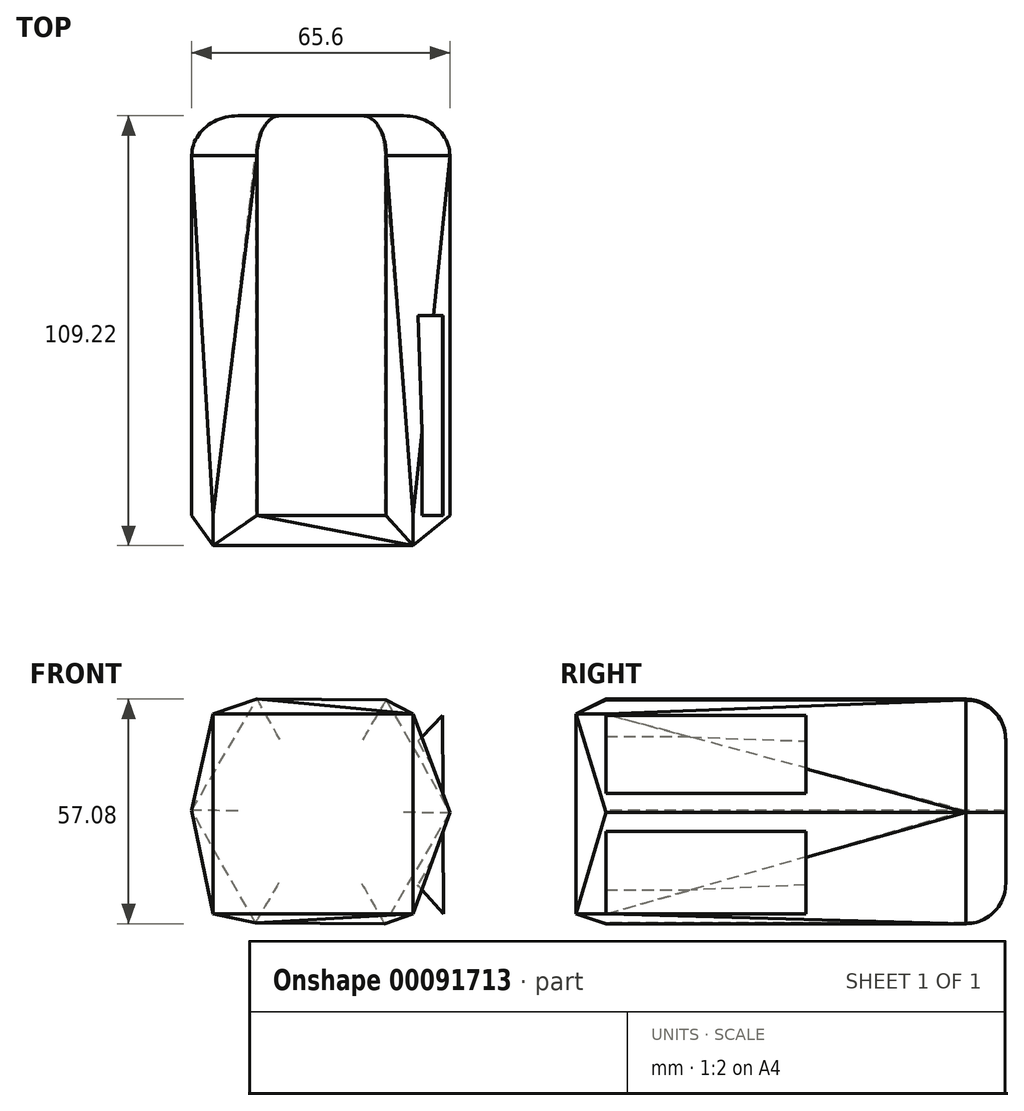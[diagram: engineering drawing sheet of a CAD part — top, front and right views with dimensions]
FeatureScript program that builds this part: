
annotation { "Feature Type Name" : "Feature", "Feature Type Description" : "" }
export const myFeature = defineFeature(function(context is Context, id is Id, definition is map)
    precondition{}
    {
        {
            var Q0;
            Q0=qCreatedBy(makeId("Front.planeOp"),FACE);
            var sketch = newSketch(context, id + "F0", { "sketchPlane" : qUnion([Q0])});
            skCircle(sketch, "E0.cCircle", {"center": v(0, 0) * mm, "radius": 32.8 * mm, "construction": true});
            skLineSegment(sketch, "E0.0", {"start": v(16.18, -28.54) * mm, "end": v(-16.62, -28.28) * mm});
            skLineSegment(sketch, "E0.1", {"start": v(-16.62, -28.28) * mm, "end": v(-32.8, 0.25) * mm});
            skLineSegment(sketch, "E0.2", {"start": v(-32.8, 0.25) * mm, "end": v(-16.18, 28.54) * mm});
            skLineSegment(sketch, "E0.3", {"start": v(-16.18, 28.54) * mm, "end": v(16.62, 28.28) * mm});
            skLineSegment(sketch, "E0.4", {"start": v(16.62, 28.28) * mm, "end": v(32.8, -0.25) * mm});
            skLineSegment(sketch, "E0.5", {"start": v(32.8, -0.25) * mm, "end": v(16.18, -28.54) * mm});
            skSolve(sketch);
        }
        {
            var Q0;
            Q0=makeQuery(id+"F0.imprint","IMPRINT",FACE,{"disambiguationData":[TD([[makeQuery(id+"F0.imprint","IMPRINT",EDGE,{"derivedFrom":sQuery(id+"F0.wireOp",EDGE,"E0.0")}),-1.0]])]});
            extrude(context, id + "F1", {"entities" : qUnion([Q0]), "oppositeDirection" : true, "depth" : 101.6 * mm});
        }
        {
            var Q0;
            Q0=makeQuery(id+"F1.opExtrude","CAP_EDGE",EDGE,{"disambiguationData":[OSD([sQuery(id+"F0.wireOp",EDGE,"E0.5")])],"isStart":false});
            var Q1;
            Q1=makeQuery(id+"F1.opExtrude","CAP_EDGE",EDGE,{"disambiguationData":[OSD([sQuery(id+"F0.wireOp",EDGE,"E0.4")])],"isStart":false});
            var Q2;
            Q2=makeQuery(id+"F1.opExtrude","CAP_EDGE",EDGE,{"disambiguationData":[OSD([sQuery(id+"F0.wireOp",EDGE,"E0.3")])],"isStart":false});
            var Q3;
            Q3=makeQuery(id+"F1.opExtrude","CAP_EDGE",EDGE,{"disambiguationData":[OSD([sQuery(id+"F0.wireOp",EDGE,"E0.2")])],"isStart":false});
            var Q4;
            Q4=makeQuery(id+"F1.opExtrude","CAP_EDGE",EDGE,{"disambiguationData":[OSD([sQuery(id+"F0.wireOp",EDGE,"E0.1")])],"isStart":false});
            var Q5;
            Q5=makeQuery(id+"F1.opExtrude","CAP_EDGE",EDGE,{"disambiguationData":[OSD([sQuery(id+"F0.wireOp",EDGE,"E0.0")])],"isStart":false});
            fillet(context, id + "F2", {"entities" : qUnion([Q0, Q1, Q2, Q3, Q4, Q5]), "radius" : 10.16 * mm, "tangentPropagation" : true, "allowEdgeOverflow" : false});
        }
        {
            var Q0;
            Q0=qCreatedBy(makeId("Front.planeOp"),FACE);
            var sketch = newSketch(context, id + "F3", { "sketchPlane" : qUnion([Q0])});
            skLineSegment(sketch, "E1.bottom", {"start": v(-27.3, 24.74) * mm, "end": v(23.5, 24.74) * mm});
            skLineSegment(sketch, "E1.top", {"start": v(-27.3, -26.06) * mm, "end": v(23.5, -26.06) * mm});
            skLineSegment(sketch, "E1.left", {"start": v(-27.3, 24.74) * mm, "end": v(-27.3, -26.06) * mm});
            skLineSegment(sketch, "E1.right", {"start": v(23.5, 24.74) * mm, "end": v(23.5, -26.06) * mm});
            skSolve(sketch);
        }
        {
            var Q0;
            Q0=makeQuery(id+"F3.imprint","IMPRINT",FACE,{"disambiguationData":[TD([[makeQuery(id+"F3.imprint","IMPRINT",EDGE,{"derivedFrom":sQuery(id+"F3.wireOp",EDGE,"E1.bottom")}),-1.0]])]});
            extrude(context, id + "F4", {"entities" : qUnion([Q0]), "operationType" : NewBodyOperationType.ADD, "depth" : 7.62 * mm});
        }
        {
            var Q1;
            Q1=makeQuery(id+"F1.opExtrude","CAP_VERTEX",VERTEX,{"disambiguationData":[OSD([sQuery(id+"F0.wireOp",EDGE,"E0.0"),sQuery(id+"F0.wireOp",EDGE,"E0.1")])],"isStart":true});
            var Q2;
            Q2=makeQuery(id+"F4.opExtrude","SWEPT_FACE",FACE,{"disambiguationData":[OSD([sQuery(id+"F3.wireOp",EDGE,"E1.top")])]});
            loft(context, id + "F5", {"operationType" : NewBodyOperationType.ADD, "sheetProfilesArray" : [{ "sheetProfileEntities" : qUnion([Q1]) }, { "sheetProfileEntities" : qUnion([Q2]) }]});
        }
        {
            var Q1;
            Q1=makeQuery(id+"F1.opExtrude","CAP_VERTEX",VERTEX,{"disambiguationData":[OSD([sQuery(id+"F0.wireOp",EDGE,"E0.0"),sQuery(id+"F0.wireOp",EDGE,"E0.5")])],"isStart":true});
            var Q2;
            Q2=makeQuery(id+"F5.opLoft","SWEPT_FACE",FACE,{"disambiguationData":[OSD([sQuery(id+"F3.wireOp",EDGE,"E1.top"),sQuery(id+"F3.wireOp",EDGE,"E1.right")])]});
            loft(context, id + "F6", {"operationType" : NewBodyOperationType.ADD, "sheetProfilesArray" : [{ "sheetProfileEntities" : qUnion([Q1]) }, { "sheetProfileEntities" : qUnion([Q2]) }]});
        }
        {
            var Q1;
            {var subQ0=sQuery(id+"F3.wireOp",EDGE,"E1.left");var subQ1=sQuery(id+"F3.wireOp",EDGE,"E1.top");var subQ2=makeQuery(id+"F4.opExtrude","CAP_VERTEX",VERTEX,{"disambiguationData":[OSD([subQ1,subQ0])],"isStart":true});Q1=makeQuery(id+"F5.boolean.opBoolean","MERGE",VERTEX,{"derivedFrom":[subQ2,makeQuery(id+"F5.opLoft","MID_CAP_VERTEX",VERTEX,{"disambiguationData":[OSD([subQ1,subQ0]),TDD([subQ2])],"capPos":1.0})]});}
            var Q2;
            Q2=makeQuery(id+"F1.opExtrude","SWEPT_FACE",FACE,{"disambiguationData":[OSD([sQuery(id+"F0.wireOp",EDGE,"E0.1")])]});
            loft(context, id + "F7", {"operationType" : NewBodyOperationType.ADD, "sheetProfilesArray" : [{ "sheetProfileEntities" : qUnion([Q1]) }, { "sheetProfileEntities" : qUnion([Q2]) }]});
        }
        {
            var Q1;
            {var subQ0=sQuery(id+"F3.wireOp",EDGE,"E1.right");var subQ1=sQuery(id+"F3.wireOp",EDGE,"E1.top");var subQ2=makeQuery(id+"F4.opExtrude","CAP_VERTEX",VERTEX,{"disambiguationData":[OSD([subQ1,subQ0])],"isStart":true});var subQ3=makeQuery(id+"F5.boolean.opBoolean","MERGE",VERTEX,{"derivedFrom":[subQ2,makeQuery(id+"F5.opLoft","MID_CAP_VERTEX",VERTEX,{"disambiguationData":[OSD([subQ1,subQ0]),TDD([subQ2])],"capPos":1.0})]});Q1=makeQuery(id+"F6.boolean.opBoolean","MERGE",VERTEX,{"derivedFrom":[subQ3,makeQuery(id+"F6.opLoft","MID_CAP_VERTEX",VERTEX,{"disambiguationData":[OSD([subQ1,subQ0]),TDD([subQ3])],"capPos":1.0})]});}
            var Q2;
            Q2=makeQuery(id+"F1.opExtrude","SWEPT_FACE",FACE,{"disambiguationData":[OSD([sQuery(id+"F0.wireOp",EDGE,"E0.5")])]});
            loft(context, id + "F8", {"operationType" : NewBodyOperationType.ADD, "sheetProfilesArray" : [{ "sheetProfileEntities" : qUnion([Q1]) }, { "sheetProfileEntities" : qUnion([Q2]) }]});
        }
        {
            var Q1;
            Q1=makeQuery(id+"F4.opExtrude","SWEPT_FACE",FACE,{"disambiguationData":[OSD([sQuery(id+"F3.wireOp",EDGE,"E1.right")])]});
            var Q2;
            {var subQ0=sQuery(id+"F0.wireOp",EDGE,"E0.5");var subQ1=sQuery(id+"F0.wireOp",EDGE,"E0.4");var subQ2=makeQuery(id+"F1.opExtrude","CAP_VERTEX",VERTEX,{"disambiguationData":[OSD([subQ1,subQ0])],"isStart":true});Q2=makeQuery(id+"F8.boolean.opBoolean","MERGE",VERTEX,{"derivedFrom":[subQ2,makeQuery(id+"F8.opLoft","MID_CAP_VERTEX",VERTEX,{"disambiguationData":[OSD([subQ1,subQ0]),TDD([subQ2])],"capPos":1.0})]});}
            loft(context, id + "F9", {"operationType" : NewBodyOperationType.ADD, "sheetProfilesArray" : [{ "sheetProfileEntities" : qUnion([Q1]) }, { "sheetProfileEntities" : qUnion([Q2]) }]});
        }
        {
            var Q1;
            Q1=makeQuery(id+"F1.opExtrude","CAP_VERTEX",VERTEX,{"disambiguationData":[OSD([sQuery(id+"F0.wireOp",EDGE,"E0.2"),sQuery(id+"F0.wireOp",EDGE,"E0.3")])],"isStart":true});
            var Q2;
            Q2=makeQuery(id+"F4.opExtrude","SWEPT_FACE",FACE,{"disambiguationData":[OSD([sQuery(id+"F3.wireOp",EDGE,"E1.bottom")])]});
            loft(context, id + "F10", {"operationType" : NewBodyOperationType.ADD, "sheetProfilesArray" : [{ "sheetProfileEntities" : qUnion([Q1]) }, { "sheetProfileEntities" : qUnion([Q2]) }]});
        }
        {
            var Q1;
            {var subQ0=sQuery(id+"F3.wireOp",EDGE,"E1.left");var subQ1=sQuery(id+"F3.wireOp",EDGE,"E1.bottom");var subQ2=makeQuery(id+"F4.opExtrude","CAP_VERTEX",VERTEX,{"disambiguationData":[OSD([subQ1,subQ0])],"isStart":true});Q1=makeQuery(id+"F10.boolean.opBoolean","MERGE",VERTEX,{"derivedFrom":[subQ2,makeQuery(id+"F10.opLoft","MID_CAP_VERTEX",VERTEX,{"disambiguationData":[OSD([subQ1,subQ0]),TDD([subQ2])],"capPos":1.0})]});}
            var Q2;
            Q2=makeQuery(id+"F1.opExtrude","SWEPT_FACE",FACE,{"disambiguationData":[OSD([sQuery(id+"F0.wireOp",EDGE,"E0.2")])]});
            loft(context, id + "F11", {"operationType" : NewBodyOperationType.ADD, "sheetProfilesArray" : [{ "sheetProfileEntities" : qUnion([Q1]) }, { "sheetProfileEntities" : qUnion([Q2]) }]});
        }
        {
            var Q1;
            {var subQ0=sQuery(id+"F0.wireOp",EDGE,"E0.2");var subQ1=sQuery(id+"F0.wireOp",EDGE,"E0.1");var subQ2=makeQuery(id+"F1.opExtrude","CAP_VERTEX",VERTEX,{"disambiguationData":[OSD([subQ1,subQ0])],"isStart":true});var subQ3=makeQuery(id+"F7.boolean.opBoolean","MERGE",VERTEX,{"derivedFrom":[subQ2,makeQuery(id+"F7.opLoft","MID_CAP_VERTEX",VERTEX,{"disambiguationData":[OSD([subQ1,subQ0]),TDD([subQ2])],"capPos":1.0})]});Q1=makeQuery(id+"F11.boolean.opBoolean","MERGE",VERTEX,{"derivedFrom":[subQ3,makeQuery(id+"F11.opLoft","MID_CAP_VERTEX",VERTEX,{"disambiguationData":[OSD([subQ1,subQ0]),TDD([subQ3])],"capPos":1.0})]});}
            var Q2;
            Q2=makeQuery(id+"F4.opExtrude","SWEPT_FACE",FACE,{"disambiguationData":[OSD([sQuery(id+"F3.wireOp",EDGE,"E1.left")])]});
            loft(context, id + "F12", {"operationType" : NewBodyOperationType.ADD, "sheetProfilesArray" : [{ "sheetProfileEntities" : qUnion([Q1]) }, { "sheetProfileEntities" : qUnion([Q2]) }]});
        }
        {
            var Q1;
            Q1=makeQuery(id+"F1.opExtrude","CAP_VERTEX",VERTEX,{"disambiguationData":[OSD([sQuery(id+"F0.wireOp",EDGE,"E0.3"),sQuery(id+"F0.wireOp",EDGE,"E0.4")])],"isStart":true});
            var Q2;
            Q2=makeQuery(id+"F10.opLoft","SWEPT_FACE",FACE,{"disambiguationData":[OSD([sQuery(id+"F3.wireOp",EDGE,"E1.bottom"),sQuery(id+"F3.wireOp",EDGE,"E1.right")])]});
            loft(context, id + "F13", {"operationType" : NewBodyOperationType.ADD, "sheetProfilesArray" : [{ "sheetProfileEntities" : qUnion([Q1]) }, { "sheetProfileEntities" : qUnion([Q2]) }]});
        }
        {
            var Q1;
            {var subQ0=sQuery(id+"F3.wireOp",EDGE,"E1.right");var subQ1=sQuery(id+"F3.wireOp",EDGE,"E1.bottom");var subQ2=makeQuery(id+"F4.opExtrude","CAP_VERTEX",VERTEX,{"disambiguationData":[OSD([subQ1,subQ0])],"isStart":true});var subQ3=makeQuery(id+"F9.boolean.opBoolean","MERGE",VERTEX,{"derivedFrom":[subQ2,makeQuery(id+"F9.opLoft","MID_CAP_VERTEX",VERTEX,{"disambiguationData":[OSD([subQ1,subQ0]),TDD([subQ2])],"capPos":0.0})]});var subQ4=makeQuery(id+"F10.boolean.opBoolean","MERGE",VERTEX,{"derivedFrom":[subQ3,makeQuery(id+"F10.opLoft","MID_CAP_VERTEX",VERTEX,{"disambiguationData":[OSD([subQ1,subQ0]),TDD([subQ3])],"capPos":1.0})]});Q1=makeQuery(id+"F13.boolean.opBoolean","MERGE",VERTEX,{"derivedFrom":[subQ4,makeQuery(id+"F13.opLoft","MID_CAP_VERTEX",VERTEX,{"disambiguationData":[OSD([subQ1,subQ0]),TDD([subQ4])],"capPos":1.0})]});}
            var Q2;
            Q2=makeQuery(id+"F1.opExtrude","SWEPT_FACE",FACE,{"disambiguationData":[OSD([sQuery(id+"F0.wireOp",EDGE,"E0.4")])]});
            loft(context, id + "F14", {"operationType" : NewBodyOperationType.ADD, "sheetProfilesArray" : [{ "sheetProfileEntities" : qUnion([Q1]) }, { "sheetProfileEntities" : qUnion([Q2]) }]});
        }
        {
            var Q0;
            Q0=qCreatedBy(makeId("Front.planeOp"),FACE);
            var sketch = newSketch(context, id + "F15", { "sketchPlane" : qUnion([Q0])});
            skLineSegment(sketch, "E2", {"start": v(31.2, -25.96) * mm, "end": v(7.48, 0) * mm});
            skLineSegment(sketch, "E3", {"start": v(7.48, 0) * mm, "end": v(30.91, 24.35) * mm});
            skLineSegment(sketch, "E4", {"start": v(30.91, 24.35) * mm, "end": v(31.2, -25.96) * mm});
            skSolve(sketch);
        }
        {
            var Q0;
            Q0=makeQuery(id+"F15.imprint","IMPRINT",FACE,{"disambiguationData":[TD([[makeQuery(id+"F15.imprint","IMPRINT",EDGE,{"derivedFrom":sQuery(id+"F15.wireOp",EDGE,"E2")}),-1.0]])]});
            extrude(context, id + "F16", {"entities" : qUnion([Q0]), "operationType" : NewBodyOperationType.ADD, "oppositeDirection" : true, "depth" : 50.8 * mm});
        }
    });
